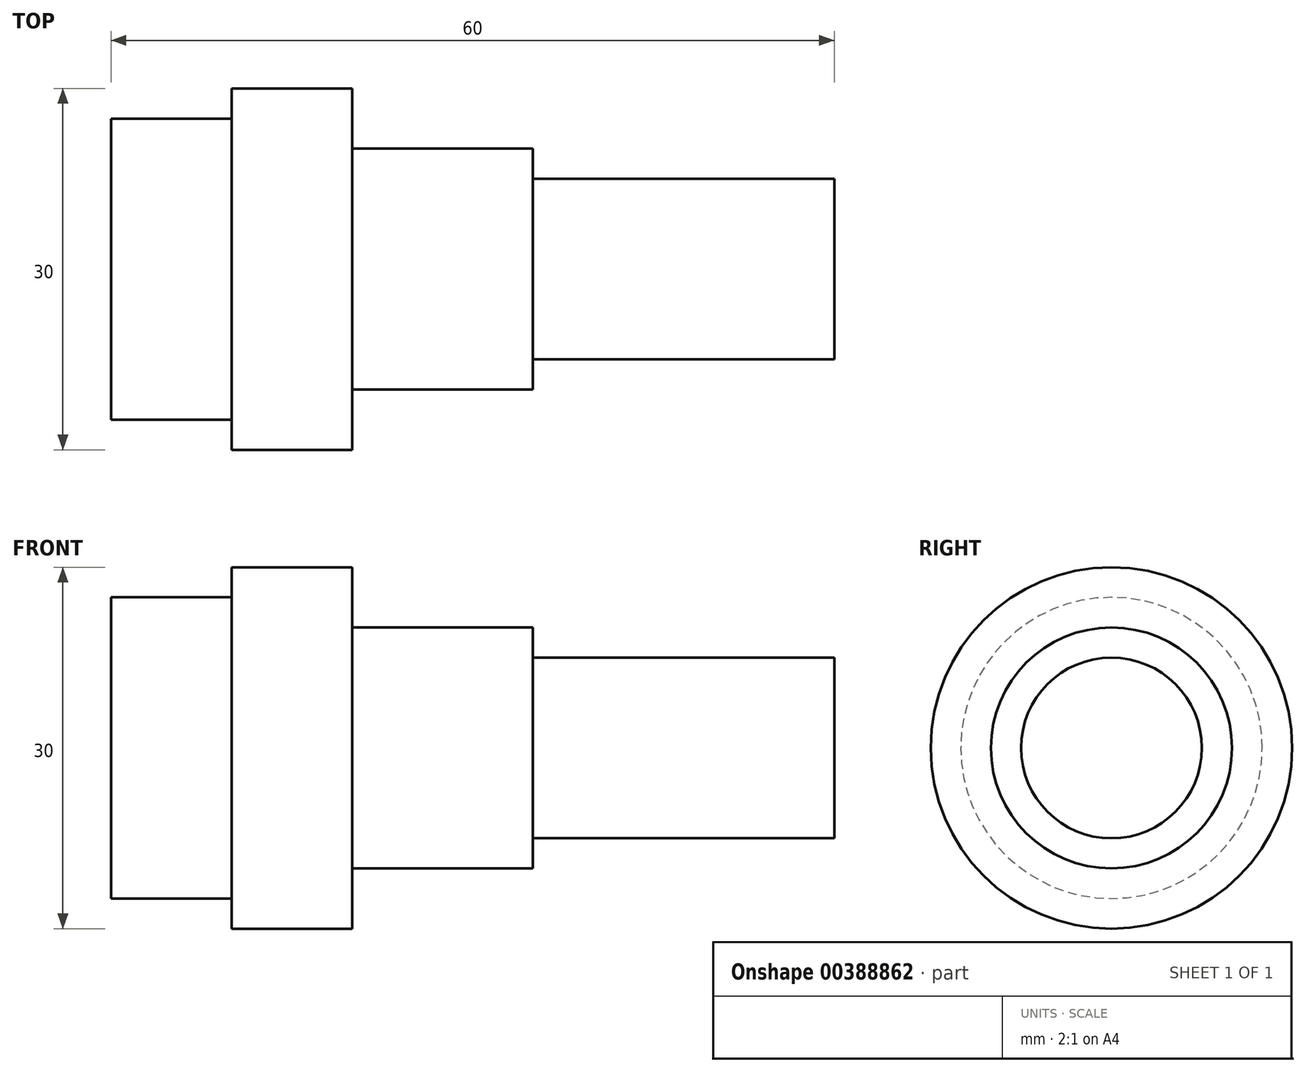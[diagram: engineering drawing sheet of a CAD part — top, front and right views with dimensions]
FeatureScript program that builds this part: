
annotation { "Feature Type Name" : "Feature", "Feature Type Description" : "" }
export const myFeature = defineFeature(function(context is Context, id is Id, definition is map)
    precondition{}
    {
        {
            var Q0;
            Q0=qCreatedBy(makeId("Top.planeOp"),FACE);
            var sketch = newSketch(context, id + "F0", { "sketchPlane" : qUnion([Q0])});
            skLineSegment(sketch, "E0", {"start": v(25, 0) * mm, "end": v(25, 7.5) * mm});
            skLineSegment(sketch, "E1", {"start": v(0, 7.5) * mm, "end": v(25, 7.5) * mm});
            skLineSegment(sketch, "E2", {"start": v(0, 7.5) * mm, "end": v(0, 10) * mm});
            skLineSegment(sketch, "E3", {"start": v(0, 10) * mm, "end": v(-15, 10) * mm});
            skLineSegment(sketch, "E4", {"start": v(-15, 10) * mm, "end": v(-15, 15) * mm});
            skLineSegment(sketch, "E5", {"start": v(-15, 15) * mm, "end": v(-25, 15) * mm});
            skLineSegment(sketch, "E6", {"start": v(-25, 15) * mm, "end": v(-25, 12.5) * mm});
            skLineSegment(sketch, "E7", {"start": v(-25, 12.5) * mm, "end": v(-35, 12.5) * mm});
            skLineSegment(sketch, "E8", {"start": v(-35, 12.5) * mm, "end": v(-35, 0) * mm});
            skLineSegment(sketch, "E9", {"start": v(-41.09, 0) * mm, "end": v(34.5, 0) * mm, "construction": true});
            skLineSegment(sketch, "E10", {"start": v(-35, 0) * mm, "end": v(25, 0) * mm});
            skSolve(sketch);
        }
        {
            var Q0;
            Q0 = qSketchRegion(id + "F0", true);
            var Q1;
            Q1=sQuery(id+"F0.wireOp",EDGE,"E9");
            revolve(context, id + "F1", {"entities" : qUnion([Q0]), "axis" : qUnion([Q1]), "revolveType" : RevolveType.FULL});
        }
    });
